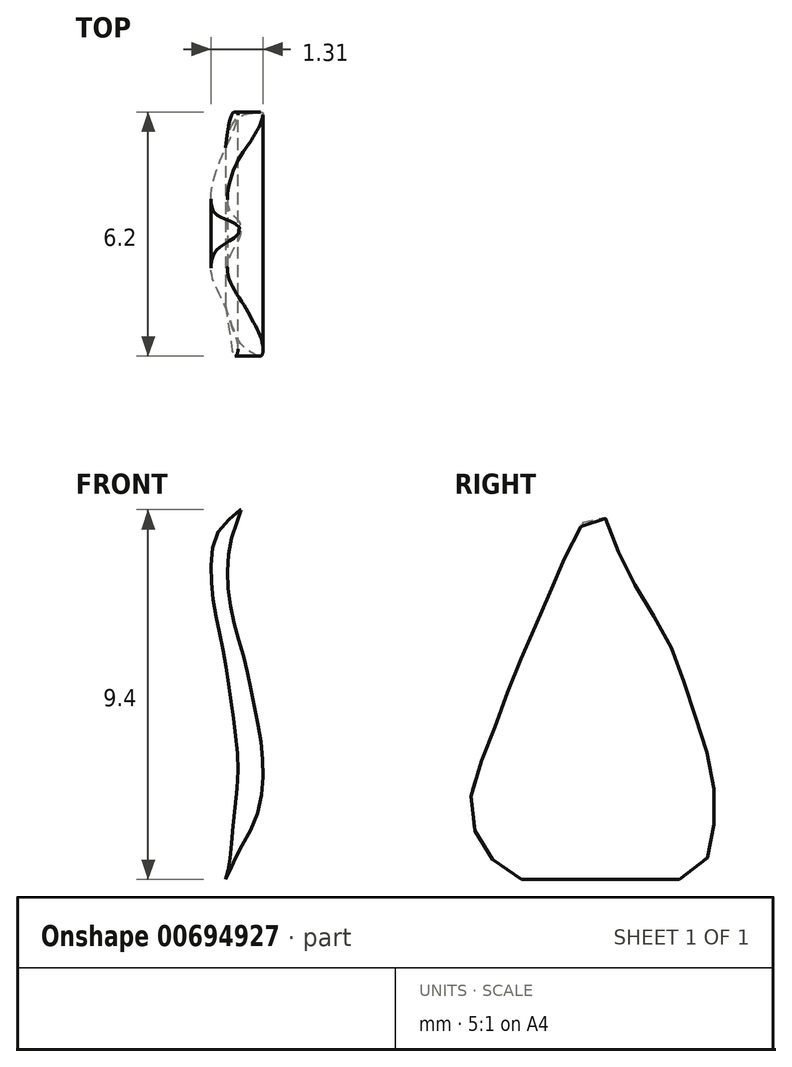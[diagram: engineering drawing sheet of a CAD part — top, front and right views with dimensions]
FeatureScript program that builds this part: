
annotation { "Feature Type Name" : "Feature", "Feature Type Description" : "" }
export const myFeature = defineFeature(function(context is Context, id is Id, definition is map)
    precondition{}
    {
        {
            var Q0;
            Q0=qCreatedBy(makeId("Right.planeOp"),FACE);
            var sketch = newSketch(context, id + "F0", { "sketchPlane" : qUnion([Q0])});
            skPoint(sketch, "E0", {"position": v(0, 0) * mm});
            skFitSpline(sketch, "E1", {"points": [v(0, 6.68) * mm, v(0.59, 5.56) * mm, v(1.87, 3.28) * mm, v(2.34, 1.97) * mm, v(2.94, 0) * mm, v(2.98, -1.36) * mm, v(2.54, -2.5) * mm, v(0, -2.97) * mm, v(-1.36, -2.9) * mm, v(-2.74, -2.08) * mm, v(-3.18, -0.64) * mm, v(-2.75, 0.7) * mm, v(-2.24, 2.07) * mm, v(-1.79, 3.16) * mm, v(-1.21, 4.48) * mm, v(0, 6.68) * mm]});
            skSolve(sketch);
        }
        {
            var Q0;
            Q0=makeQuery(id+"F0.imprint","IMPRINT",FACE,{"disambiguationData":[TD([[makeQuery(id+"F0.imprint","IMPRINT",EDGE,{"derivedFrom":sQuery(id+"F0.wireOp",EDGE,"E1")}),-1.0]])]});
            extrude(context, id + "F1", {"entities" : qUnion([Q0]), "oppositeDirection" : true, "depth" : 2 * mm, "offsetDistance" : 25 * mm});
        }
        {
            var Q0;
            Q0=qCreatedBy(makeId("Front.planeOp"),FACE);
            var sketch = newSketch(context, id + "F2", { "sketchPlane" : qUnion([Q0])});
            skFitSpline(sketch, "E2", {"points": [v(-1.27, -3.02) * mm, v(-0.72, -1.95) * mm, v(-0.27, -1.02) * mm, v(-0.15, 0.39) * mm, v(-0.34, 1.63) * mm, v(-0.58, 2.77) * mm, v(-0.86, 3.8) * mm, v(-1.03, 4.77) * mm, v(-0.96, 5.86) * mm, v(-0.7, 6.67) * mm, v(-0.48, 7.15) * mm, v(1.47, 5.94) * mm, v(1.61, -2.23) * mm, v(1.04, -4.14) * mm, v(-1.43, -3.42) * mm, v(-1.27, -3.02) * mm]});
            skFitSpline(sketch, "E3", {"points": [v(-0.64, 6.94) * mm, v(-1.15, 6.3) * mm, v(-1.43, 5.56) * mm, v(-1.41, 4.44) * mm, v(-1.15, 3.1) * mm, v(-0.91, 1.55) * mm, v(-0.77, 0) * mm, v(-0.89, -1.2) * mm, v(-1.43, -3.42) * mm, v(-3, -3.64) * mm, v(-3.48, 4.1) * mm, v(-2.7, 7.48) * mm, v(-0.64, 6.94) * mm]});
            skSolve(sketch);
        }
        {
            var Q0;
            Q0=qSketchRegion(id+"F2",true);
            extrude(context, id + "F3", {"entities" : qUnion([Q0]), "operationType" : NewBodyOperationType.REMOVE, "oppositeDirection" : true, "depth" : 8 * mm, "offsetDistance" : 25 * mm, "symmetric" : true});
        }
        {
            var Q0;
            Q0=makeQuery(id+"F1.opExtrude","SWEPT_BODY",BODY,{"disambiguationData":[OSD([sQuery(id+"F0.wireOp",EDGE,"E1")])]});
            transform(context, id + "F4", {"entities" : qUnion([Q0]), "transformType" : TransformType.TRANSLATION_3D, "dx" : 0 * mm, "dy" : 0 * mm, "dz" : 0 * mm, "makeCopy" : true});
        }
    });
